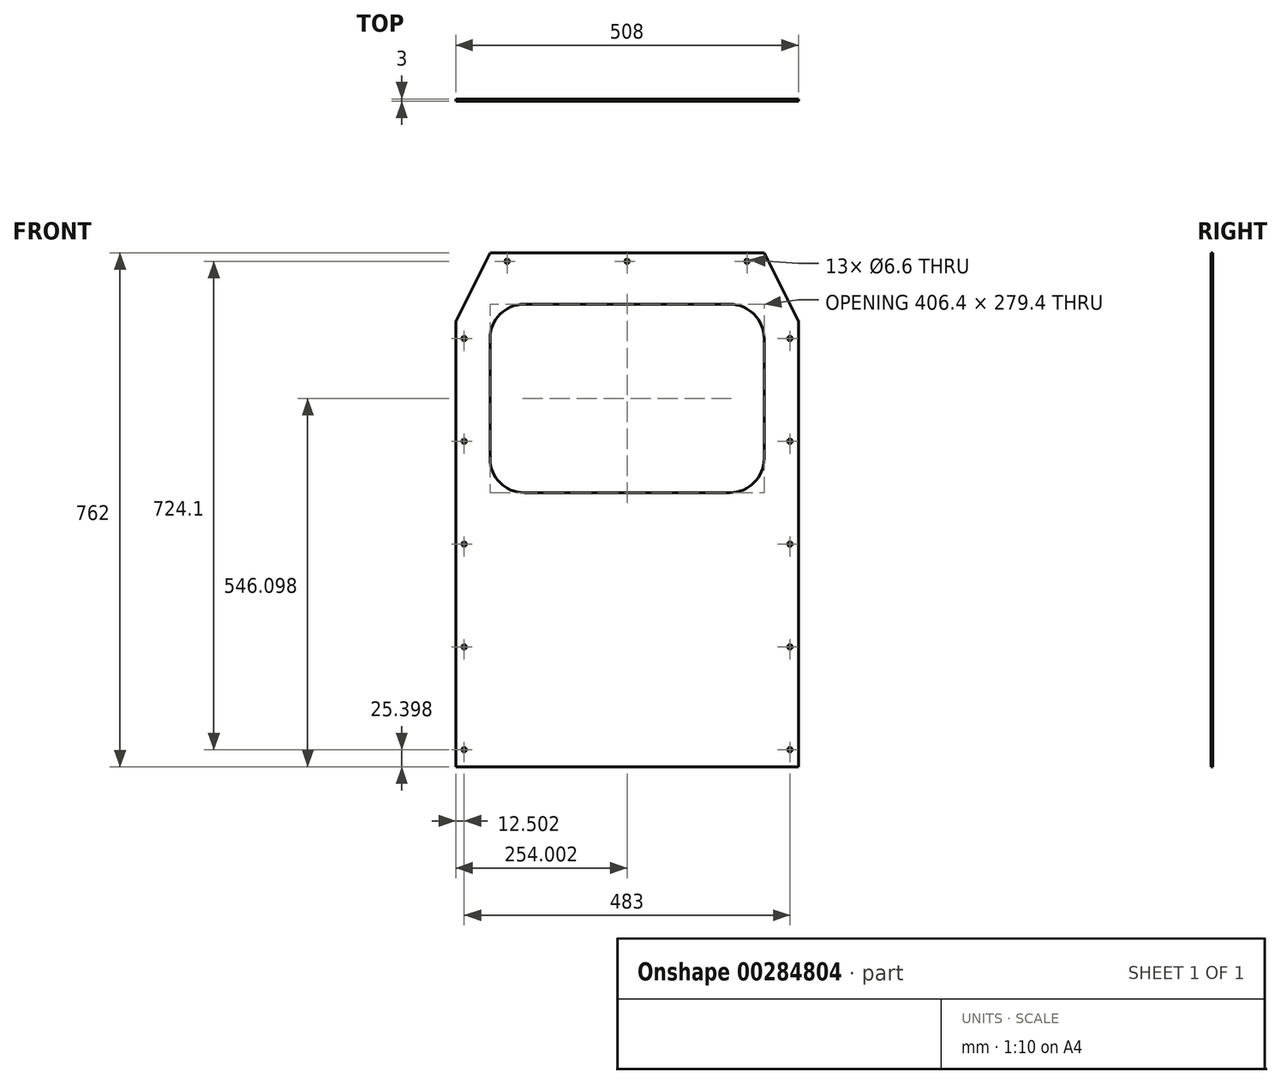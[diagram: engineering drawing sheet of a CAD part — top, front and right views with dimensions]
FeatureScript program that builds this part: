
annotation { "Feature Type Name" : "Feature", "Feature Type Description" : "" }
export const myFeature = defineFeature(function(context is Context, id is Id, definition is map)
    precondition{}
    {
        {
            var Q0;
            Q0=qCreatedBy(makeId("Front.planeOp"),FACE);
            var sketch = newSketch(context, id + "F0", { "sketchPlane" : qUnion([Q0])});
            skLineSegment(sketch, "E0", {"start": v(-236.26, -523.3) * mm, "end": v(271.74, -523.3) * mm});
            skLineSegment(sketch, "E1", {"start": v(271.74, -523.3) * mm, "end": v(271.74, 137.1) * mm});
            skLineSegment(sketch, "E2", {"start": v(271.74, 137.1) * mm, "end": v(220.94, 238.7) * mm});
            skLineSegment(sketch, "E3", {"start": v(220.94, 238.7) * mm, "end": v(-185.46, 238.7) * mm});
            skLineSegment(sketch, "E4", {"start": v(-185.46, 238.7) * mm, "end": v(-236.26, 137.1) * mm});
            skLineSegment(sketch, "E5", {"start": v(-236.26, 137.1) * mm, "end": v(-236.26, -523.3) * mm});
            skLineSegment(sketch, "E6.bottom", {"start": v(-134.66, 162.5) * mm, "end": v(170.14, 162.5) * mm});
            skLineSegment(sketch, "E6.top", {"start": v(-134.66, -116.9) * mm, "end": v(170.14, -116.9) * mm});
            skLineSegment(sketch, "E6.left", {"start": v(-185.46, 111.7) * mm, "end": v(-185.46, -66.1) * mm});
            skLineSegment(sketch, "E6.right", {"start": v(220.94, 111.7) * mm, "end": v(220.94, -66.1) * mm});
            skPoint(sketch, "E7.visualSharp", {"position": v(-185.46, 162.5) * mm});
            skArc(sketch, "E7.filletArc", {"start": v(-134.66, 162.5) * mm, "mid": v(-170.58, 147.63) * mm, "end": v(-185.46, 111.7) * mm});
            skPoint(sketch, "E8.visualSharp", {"position": v(220.94, 162.5) * mm});
            skArc(sketch, "E8.filletArc", {"start": v(220.94, 111.7) * mm, "mid": v(206.06, 147.63) * mm, "end": v(170.14, 162.5) * mm});
            skPoint(sketch, "E9.visualSharp", {"position": v(220.94, -116.9) * mm});
            skArc(sketch, "E9.filletArc", {"start": v(170.14, -116.9) * mm, "mid": v(206.06, -102.01) * mm, "end": v(220.94, -66.1) * mm});
            skPoint(sketch, "E10.visualSharp", {"position": v(-185.46, -116.9) * mm});
            skArc(sketch, "E10.filletArc", {"start": v(-185.46, -66.1) * mm, "mid": v(-170.58, -102.01) * mm, "end": v(-134.66, -116.9) * mm});
            skSolve(sketch);
        }
        {
            var Q0;
            Q0 = qSketchRegion(id + "F0", true);
            extrude(context, id + "F1", {"entities" : qUnion([Q0]), "depth" : 3 * mm});
        }
        {
            var Q0;
            Q0=makeQuery(id+"F1.opExtrude","CAP_FACE",FACE,{"disambiguationData":[OSD([sQuery(id+"F0.wireOp",EDGE,"E0"),sQuery(id+"F0.wireOp",EDGE,"E1"),sQuery(id+"F0.wireOp",EDGE,"E2"),sQuery(id+"F0.wireOp",EDGE,"E3"),sQuery(id+"F0.wireOp",EDGE,"E4"),sQuery(id+"F0.wireOp",EDGE,"E5"),sQuery(id+"F0.wireOp",EDGE,"E6.bottom"),sQuery(id+"F0.wireOp",EDGE,"E6.top"),sQuery(id+"F0.wireOp",EDGE,"E6.left"),sQuery(id+"F0.wireOp",EDGE,"E6.right"),sQuery(id+"F0.wireOp",EDGE,"E7.filletArc"),sQuery(id+"F0.wireOp",EDGE,"E8.filletArc"),sQuery(id+"F0.wireOp",EDGE,"E9.filletArc"),sQuery(id+"F0.wireOp",EDGE,"E10.filletArc")])],"isStart":false});
            var sketch = newSketch(context, id + "F2", { "sketchPlane" : qUnion([Q0])});
            skPoint(sketch, "E11", {"position": v(-223.76, 111.7) * mm});
            skPoint(sketch, "E12", {"position": v(-223.76, -40.7) * mm});
            skPoint(sketch, "E13", {"position": v(-223.76, -193.1) * mm});
            skPoint(sketch, "E14", {"position": v(-223.76, -345.5) * mm});
            skPoint(sketch, "E15", {"position": v(-223.76, -497.9) * mm});
            skPoint(sketch, "E16", {"position": v(259.24, 111.7) * mm});
            skPoint(sketch, "E17", {"position": v(259.24, -40.7) * mm});
            skPoint(sketch, "E18", {"position": v(259.24, -193.1) * mm});
            skPoint(sketch, "E19", {"position": v(259.24, -345.5) * mm});
            skPoint(sketch, "E20", {"position": v(259.24, -497.9) * mm});
            skPoint(sketch, "E21", {"position": v(195.54, 226.2) * mm});
            skPoint(sketch, "E22", {"position": v(-160.06, 226.2) * mm});
            skPoint(sketch, "E23", {"position": v(17.74, 226.2) * mm});
            skSolve(sketch);
        }
        {
            var Q0;
            Q0=sQuery(id+"F2.wireOp",VERTEX,"E15");
            var Q1;
            Q1=sQuery(id+"F2.wireOp",VERTEX,"E14");
            var Q2;
            Q2=sQuery(id+"F2.wireOp",VERTEX,"E13");
            var Q3;
            Q3=sQuery(id+"F2.wireOp",VERTEX,"E12");
            var Q4;
            Q4=sQuery(id+"F2.wireOp",VERTEX,"E11");
            var Q5;
            Q5=sQuery(id+"F2.wireOp",VERTEX,"E22");
            var Q6;
            Q6=sQuery(id+"F2.wireOp",VERTEX,"E23");
            var Q7;
            Q7=sQuery(id+"F2.wireOp",VERTEX,"E21");
            var Q8;
            Q8=sQuery(id+"F2.wireOp",VERTEX,"E16");
            var Q9;
            Q9=sQuery(id+"F2.wireOp",VERTEX,"E17");
            var Q10;
            Q10=sQuery(id+"F2.wireOp",VERTEX,"E18");
            var Q11;
            Q11=sQuery(id+"F2.wireOp",VERTEX,"E19");
            var Q12;
            Q12=sQuery(id+"F2.wireOp",VERTEX,"E20");
            var Q13;
            Q13=makeQuery(id+"F1.opExtrude","SWEPT_BODY",BODY,{"disambiguationData":[OSD([sQuery(id+"F0.wireOp",EDGE,"E0"),sQuery(id+"F0.wireOp",EDGE,"E1"),sQuery(id+"F0.wireOp",EDGE,"E2"),sQuery(id+"F0.wireOp",EDGE,"E3"),sQuery(id+"F0.wireOp",EDGE,"E4"),sQuery(id+"F0.wireOp",EDGE,"E5"),sQuery(id+"F0.wireOp",EDGE,"E6.bottom"),sQuery(id+"F0.wireOp",EDGE,"E6.top"),sQuery(id+"F0.wireOp",EDGE,"E6.left"),sQuery(id+"F0.wireOp",EDGE,"E6.right"),sQuery(id+"F0.wireOp",EDGE,"E7.filletArc"),sQuery(id+"F0.wireOp",EDGE,"E8.filletArc"),sQuery(id+"F0.wireOp",EDGE,"E9.filletArc"),sQuery(id+"F0.wireOp",EDGE,"E10.filletArc")])]});
            hole(context, id + "F3", {"style" : HoleStyle.SIMPLE, "endStyle" : HoleEndStyle.THROUGH, "standardTappedOrClearance" : lookupTablePath({ "standard" : "ISO", "fit" : "Normal", "size" : "M6", "type" : "Clearance" }), "standardBlindInLast" : lookupTablePath({ "fit" : "Standard", "standard" : "ISO", "size" : "M6", "type" : "Clearance" }), "holeDiameter" : 6.6 * mm, "tappedDepth" : 12 * mm, "tapClearance" : 3, "locations" : qUnion([Q0, Q1, Q2, Q3, Q4, Q5, Q6, Q7, Q8, Q9, Q10, Q11, Q12]), "scope" : qUnion([Q13])});
        }
    });
